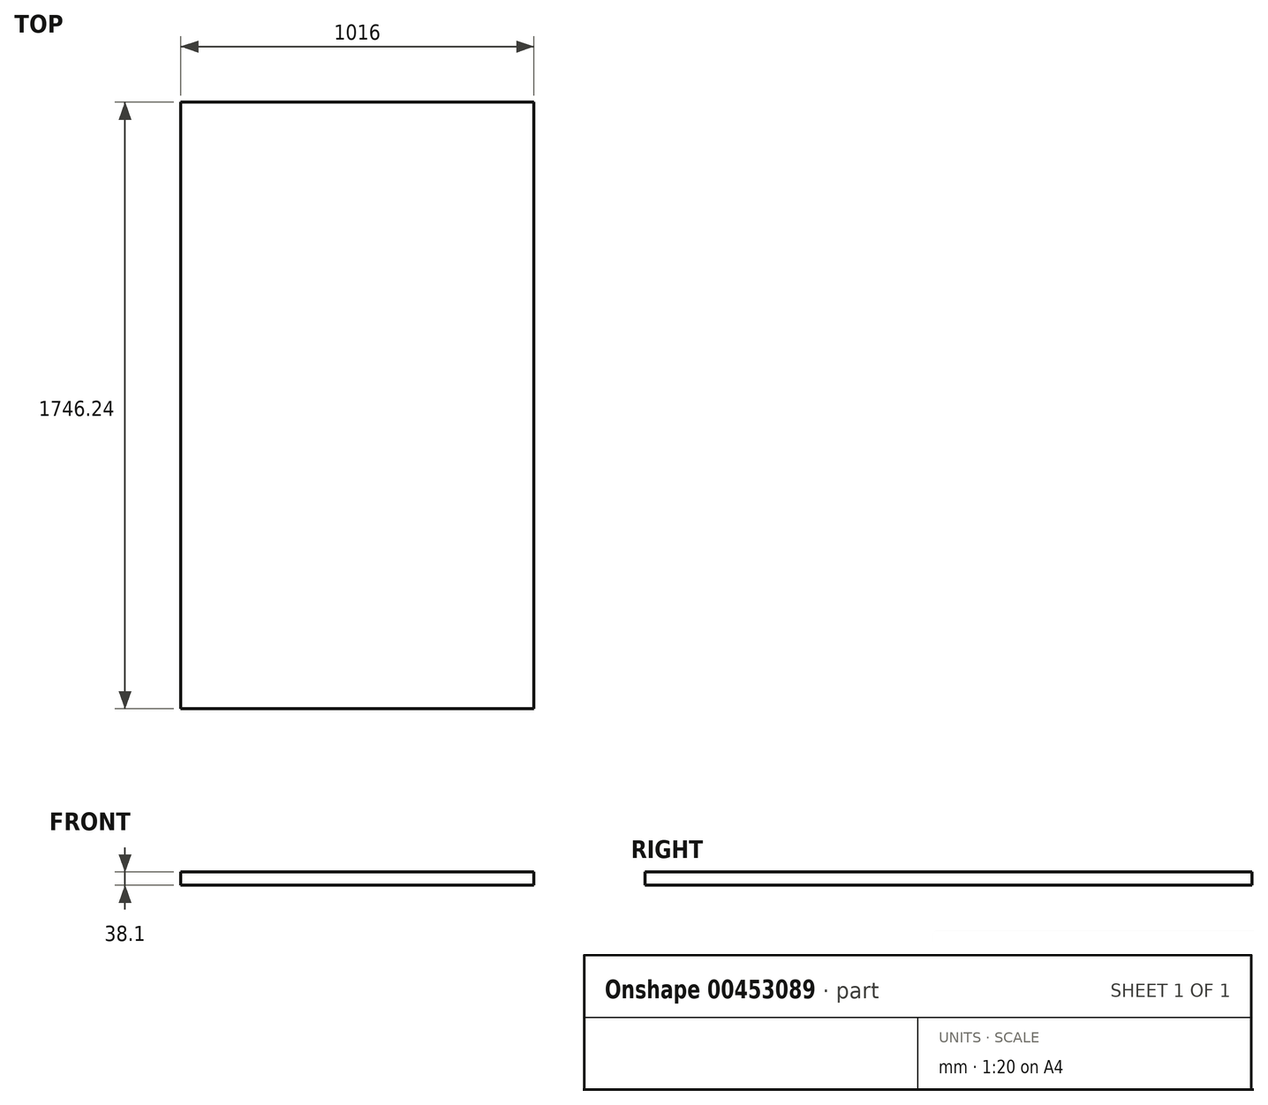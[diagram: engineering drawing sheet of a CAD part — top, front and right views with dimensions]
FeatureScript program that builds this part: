
annotation { "Feature Type Name" : "Feature", "Feature Type Description" : "" }
export const myFeature = defineFeature(function(context is Context, id is Id, definition is map)
    precondition{}
    {
        {
            var Q0;
            Q0=qCreatedBy(makeId("Top.planeOp"),FACE);
            var sketch = newSketch(context, id + "F0", { "sketchPlane" : qUnion([Q0])});
            skLineSegment(sketch, "E0.bottom", {"start": v(508, 873.12) * mm, "end": v(-508, 873.12) * mm});
            skLineSegment(sketch, "E0.top", {"start": v(508, -873.12) * mm, "end": v(-508, -873.12) * mm});
            skLineSegment(sketch, "E0.left", {"start": v(508, 873.12) * mm, "end": v(508, -873.12) * mm});
            skLineSegment(sketch, "E0.right", {"start": v(-508, 873.12) * mm, "end": v(-508, -873.12) * mm});
            skPoint(sketch, "E0.middle", {"position": v(0, 0) * mm});
            skSolve(sketch);
        }
        {
            var Q0;
            Q0 = qSketchRegion(id + "F0", true);
            extrude(context, id + "F1", {"entities" : qUnion([Q0]), "depth" : 38.1 * mm, "offsetDistance" : 25.4 * mm});
        }
    });
